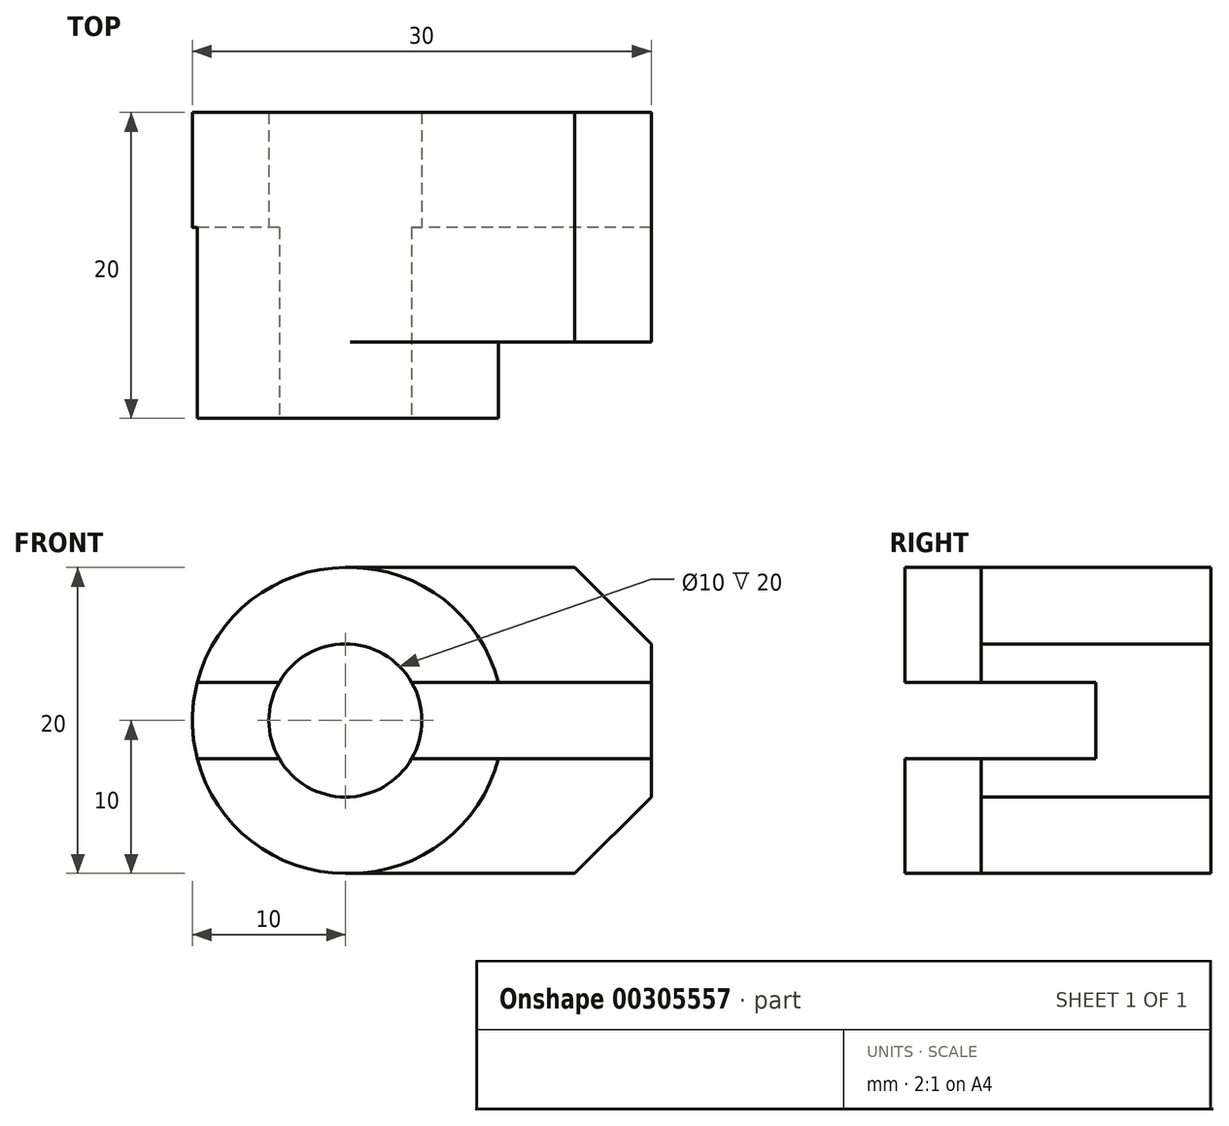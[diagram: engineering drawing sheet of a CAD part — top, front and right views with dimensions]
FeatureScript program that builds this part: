
annotation { "Feature Type Name" : "Feature", "Feature Type Description" : "" }
export const myFeature = defineFeature(function(context is Context, id is Id, definition is map)
    precondition{}
    {
        {
            var Q0;
            Q0=qCreatedBy(makeId("Top.planeOp"),FACE);
            var sketch = newSketch(context, id + "F0", { "sketchPlane" : qUnion([Q0])});
            skLineSegment(sketch, "E0", {"start": v(0, 0) * mm, "end": v(0, 20) * mm});
            skLineSegment(sketch, "E1", {"start": v(0, 20) * mm, "end": v(30, 20) * mm});
            skLineSegment(sketch, "E2", {"start": v(30, 20) * mm, "end": v(30, 5) * mm});
            skLineSegment(sketch, "E3", {"start": v(30, 5) * mm, "end": v(16.64, 5) * mm});
            skLineSegment(sketch, "E4", {"start": v(20, 5) * mm, "end": v(20, 0) * mm});
            skLineSegment(sketch, "E5", {"start": v(20, 0) * mm, "end": v(0, 0) * mm});
            skLineSegment(sketch, "E6", {"start": v(25, 20) * mm, "end": v(25, 5) * mm});
            skSolve(sketch);
        }
        {
            var Q0;
            Q0 = qSketchRegion(id + "F0", true);
            extrude(context, id + "F1", {"entities" : qUnion([Q0]), "depth" : 20 * mm});
        }
        {
            var Q0;
            Q0=makeQuery(id+"F1.opExtrude","SWEPT_FACE",FACE,{"disambiguationData":[OSD([sQuery(id+"F0.wireOp",EDGE,"E5")])]});
            var sketch = newSketch(context, id + "F2", { "sketchPlane" : qUnion([Q0])});
            skCircle(sketch, "E7", {"center": v(10, 10) * mm, "radius": 5 * mm});
            skSolve(sketch);
        }
        {
            var Q0;
            Q0 = qSketchRegion(id + "F2", true);
            extrude(context, id + "F3", {"entities" : qUnion([Q0]), "operationType" : NewBodyOperationType.REMOVE, "endBound" : BoundingType.THROUGH_ALL, "oppositeDirection" : true, "depth" : 10 * mm});
        }
        {
            var Q0;
            Q0=qCreatedBy(makeId("Right.planeOp"),FACE);
            var sketch = newSketch(context, id + "F4", { "sketchPlane" : qUnion([Q0])});
            skLineSegment(sketch, "E8", {"start": v(0, 7.5) * mm, "end": v(12.5, 7.5) * mm});
            skLineSegment(sketch, "E9", {"start": v(12.5, 7.5) * mm, "end": v(12.5, 12.5) * mm});
            skLineSegment(sketch, "E10", {"start": v(12.5, 12.5) * mm, "end": v(0, 12.5) * mm});
            skLineSegment(sketch, "E11", {"start": v(0, 12.5) * mm, "end": v(0, 7.5) * mm});
            skSolve(sketch);
        }
        {
            var Q0;
            Q0 = qSketchRegion(id + "F4", true);
            extrude(context, id + "F5", {"entities" : qUnion([Q0]), "operationType" : NewBodyOperationType.REMOVE, "endBound" : BoundingType.THROUGH_ALL, "depth" : 25 * mm});
        }
        {
            var Q0;
            Q0=makeQuery(id+"F1.opExtrude","CAP_EDGE",EDGE,{"disambiguationData":[OSD([sQuery(id+"F0.wireOp",EDGE,"E0")])],"isStart":false});
            fillet(context, id + "F6", {"entities" : qUnion([Q0]), "radius" : 10 * mm, "tangentPropagation" : true, "allowEdgeOverflow" : false});
        }
        {
            var Q0;
            Q0=makeQuery(id+"F1.opExtrude","CAP_EDGE",EDGE,{"disambiguationData":[OSD([sQuery(id+"F0.wireOp",EDGE,"E0")])],"isStart":true});
            var Q1;
            Q1=makeQuery(id+"F1.opExtrude","CAP_EDGE",EDGE,{"disambiguationData":[OSD([sQuery(id+"F0.wireOp",EDGE,"E4")])],"isStart":false});
            var Q2;
            Q2=makeQuery(id+"F1.opExtrude","CAP_EDGE",EDGE,{"disambiguationData":[OSD([sQuery(id+"F0.wireOp",EDGE,"E4")])],"isStart":true});
            fillet(context, id + "F7", {"entities" : qUnion([Q0, Q1, Q2]), "radius" : 10 * mm, "tangentPropagation" : true, "allowEdgeOverflow" : false});
        }
        {
            var Q0;
            {var subQ1=sQuery(id+"F0.wireOp",EDGE,"E3");Q0=makeQuery(id+"F5.boolean.opBoolean","SPLIT",FACE,{"disambiguationData":[TD([makeQuery(id+"F5.opExtrude","SWEPT_FACE",FACE,{"disambiguationData":[OSD([sQuery(id+"F4.wireOp",EDGE,"E8")])]})])],"derivedFrom":makeQuery(id+"F1.opExtrude","SWEPT_FACE",FACE,{"disambiguationData":[OSD([subQ1])]})});}
            var sketch = newSketch(context, id + "F8", { "sketchPlane" : qUnion([Q0])});
            skLineSegment(sketch, "E12", {"start": v(30, 5) * mm, "end": v(30, 0) * mm});
            skLineSegment(sketch, "E13", {"start": v(30, 0) * mm, "end": v(25, 0) * mm});
            skLineSegment(sketch, "E14", {"start": v(25, 0) * mm, "end": v(30, 5) * mm});
            skLineSegment(sketch, "E15", {"start": v(30, 20) * mm, "end": v(30, 15) * mm});
            skLineSegment(sketch, "E16", {"start": v(30, 15) * mm, "end": v(25, 20) * mm});
            skLineSegment(sketch, "E17", {"start": v(25, 20) * mm, "end": v(30, 20) * mm});
            skSolve(sketch);
        }
        {
            var Q0;
            Q0 = qSketchRegion(id + "F8", true);
            extrude(context, id + "F9", {"entities" : qUnion([Q0]), "operationType" : NewBodyOperationType.REMOVE, "oppositeDirection" : true, "depth" : 25 * mm});
        }
    });
